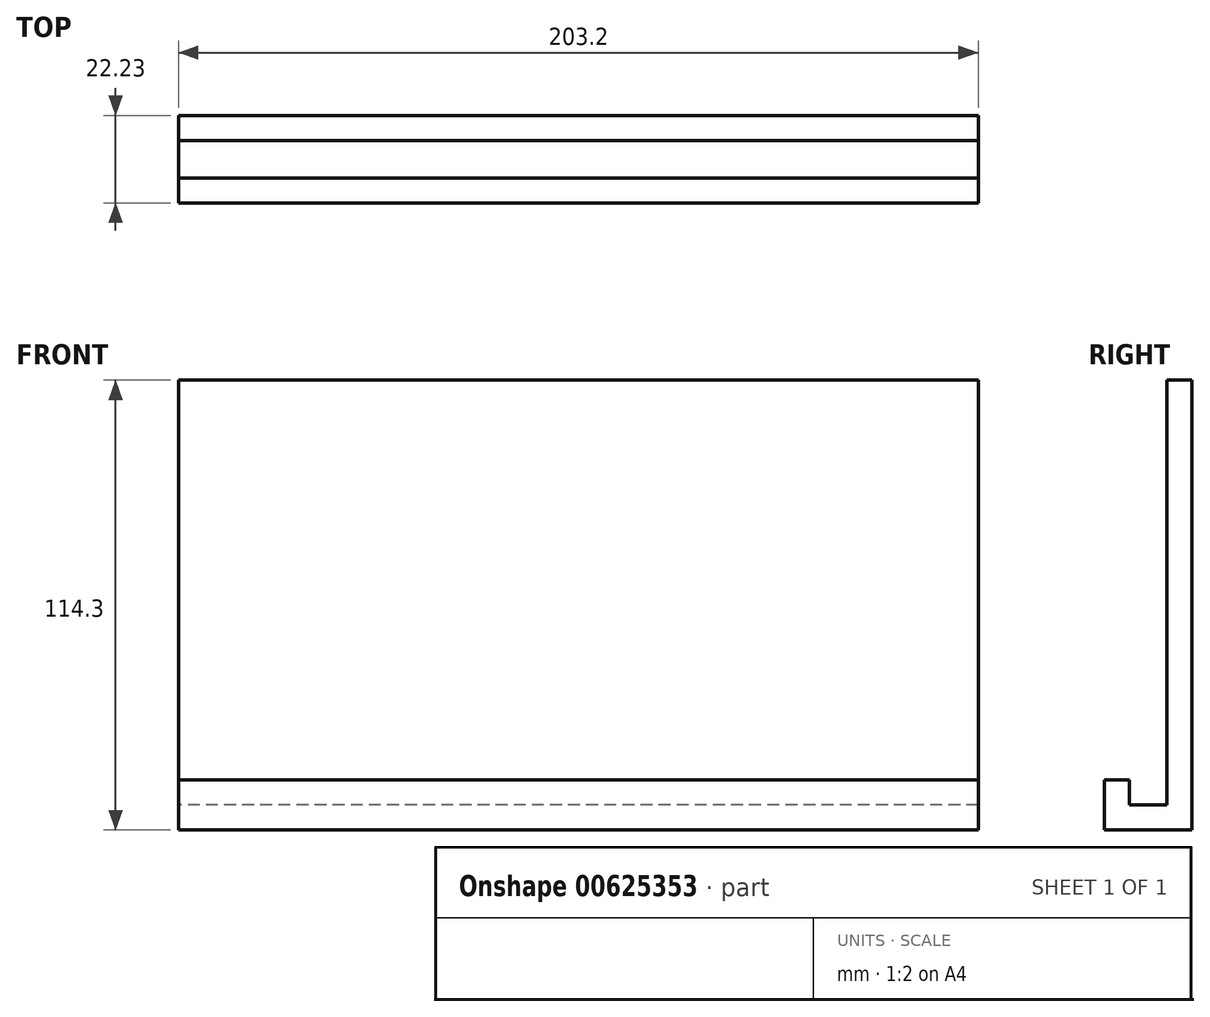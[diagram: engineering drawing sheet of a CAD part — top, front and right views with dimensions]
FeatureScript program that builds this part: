
annotation { "Feature Type Name" : "Feature", "Feature Type Description" : "" }
export const myFeature = defineFeature(function(context is Context, id is Id, definition is map)
    precondition{}
    {
        {
            var Q0;
            Q0=qCreatedBy(makeId("Right.planeOp"),FACE);
            var sketch = newSketch(context, id + "F0", { "sketchPlane" : qUnion([Q0])});
            skLineSegment(sketch, "E0", {"start": v(-15.88, -6.35) * mm, "end": v(6.35, -6.35) * mm});
            skLineSegment(sketch, "E1", {"start": v(6.35, -6.35) * mm, "end": v(6.35, 107.95) * mm});
            skLineSegment(sketch, "E2", {"start": v(6.35, 107.95) * mm, "end": v(0, 107.95) * mm});
            skLineSegment(sketch, "E3", {"start": v(0, 107.95) * mm, "end": v(0, 0) * mm});
            skLineSegment(sketch, "E4", {"start": v(0, 0) * mm, "end": v(-9.53, 0) * mm});
            skLineSegment(sketch, "E5", {"start": v(-9.53, 0) * mm, "end": v(-9.53, 6.35) * mm});
            skLineSegment(sketch, "E6", {"start": v(-9.52, 6.35) * mm, "end": v(-15.88, 6.35) * mm});
            skLineSegment(sketch, "E7", {"start": v(-15.88, 6.35) * mm, "end": v(-15.88, -6.35) * mm});
            skSolve(sketch);
        }
        {
            var Q0;
            Q0 = qSketchRegion(id + "F0", true);
            extrude(context, id + "F1", {"entities" : qUnion([Q0]), "depth" : 203.2 * mm, "offsetDistance" : 25.4 * mm, "symmetric" : true});
        }
    });
